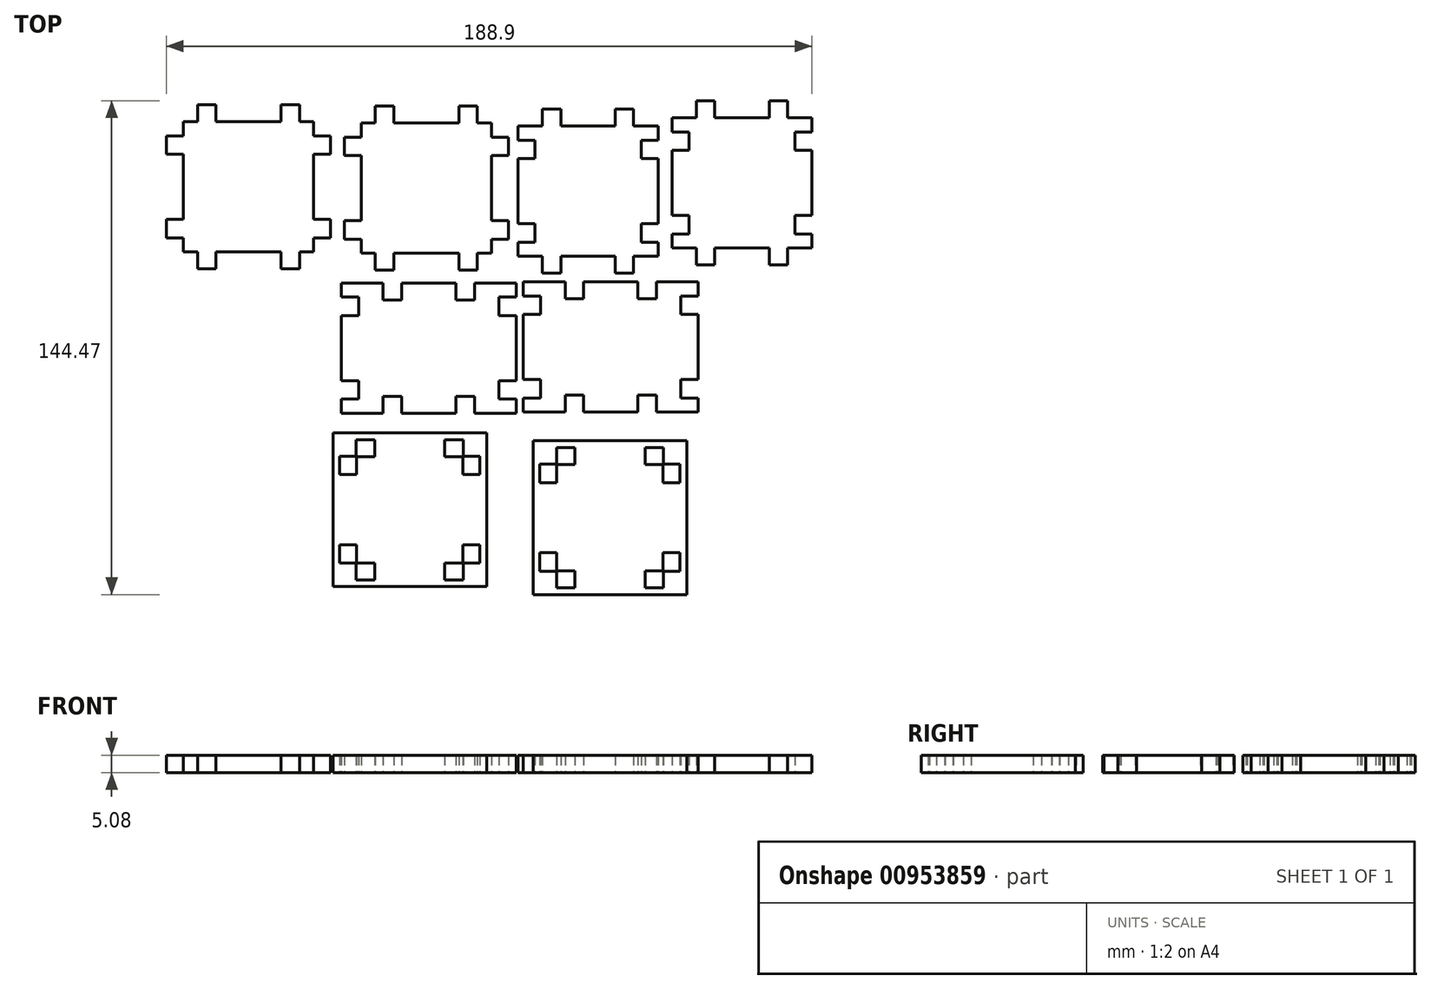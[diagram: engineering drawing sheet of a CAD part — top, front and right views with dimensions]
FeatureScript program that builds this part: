
annotation { "Feature Type Name" : "Feature", "Feature Type Description" : "" }
export const myFeature = defineFeature(function(context is Context, id is Id, definition is map)
    precondition{}
    {
        {
            var Q0;
            Q0=qCreatedBy(makeId("Top.planeOp"),FACE);
            var sketch = newSketch(context, id + "F0", { "sketchPlane" : qUnion([Q0])});
            skLineSegment(sketch, "E0", {"start": v(111.31, -90.9) * mm, "end": v(111.31, -90.9) * mm});
            skLineSegment(sketch, "E1", {"start": v(-309.98, -70.86) * mm, "end": v(-309.98, -70.86) * mm});
            skLineSegment(sketch, "E2", {"start": v(-261.6, -63.25) * mm, "end": v(-261.6, -63.25) * mm});
            skLineSegment(sketch, "E3", {"start": v(-306.4, -14.54) * mm, "end": v(-306.4, -14.54) * mm});
            skLineSegment(sketch, "E4", {"start": v(-50.36, 41.54) * mm, "end": v(-12.26, 41.54) * mm});
            skLineSegment(sketch, "E5", {"start": v(-12.26, 41.54) * mm, "end": v(-12.26, 79.64) * mm});
            skLineSegment(sketch, "E6", {"start": v(-50.36, 60.6) * mm, "end": v(-50.36, 79.64) * mm});
            skLineSegment(sketch, "E7", {"start": v(-50.36, 60.6) * mm, "end": v(-50.36, 41.54) * mm});
            skLineSegment(sketch, "E8", {"start": v(-50.36, 70.12) * mm, "end": v(-55.32, 70.12) * mm});
            skLineSegment(sketch, "E9", {"start": v(-55.32, 70.12) * mm, "end": v(-55.32, 75.52) * mm});
            skLineSegment(sketch, "E10", {"start": v(-55.32, 75.52) * mm, "end": v(-50.36, 75.52) * mm});
            skLineSegment(sketch, "E11", {"start": v(-50.36, 60.6) * mm, "end": v(-12.26, 60.6) * mm, "construction": true});
            skLineSegment(sketch, "E12", {"start": v(-31.31, 79.64) * mm, "end": v(-31.32, 41.54) * mm, "construction": true});
            skLineSegment(sketch, "E13.MirrorCS", {"start": v(-7.31, 70.11) * mm, "end": v(-7.31, 75.51) * mm});
            skLineSegment(sketch, "E14.MirrorCS", {"start": v(-7.31, 75.51) * mm, "end": v(-12.26, 75.51) * mm});
            skLineSegment(sketch, "E15.MirrorCS", {"start": v(-12.26, 70.12) * mm, "end": v(-7.31, 70.11) * mm});
            skLineSegment(sketch, "E16.MirrorCS", {"start": v(-12.27, 51.07) * mm, "end": v(-7.31, 51.07) * mm});
            skLineSegment(sketch, "E17.MirrorCS", {"start": v(-7.31, 45.67) * mm, "end": v(-12.27, 45.67) * mm});
            skLineSegment(sketch, "E18.MirrorCS", {"start": v(-7.31, 51.07) * mm, "end": v(-7.31, 45.67) * mm});
            skLineSegment(sketch, "E19.MirrorCS", {"start": v(-50.36, 51.07) * mm, "end": v(-55.32, 51.07) * mm});
            skLineSegment(sketch, "E20.MirrorCS", {"start": v(-55.32, 51.07) * mm, "end": v(-55.32, 45.67) * mm});
            skLineSegment(sketch, "E21.MirrorCS", {"start": v(-55.32, 45.67) * mm, "end": v(-50.37, 45.67) * mm});
            skLineSegment(sketch, "E22", {"start": v(-50.37, 45.67) * mm, "end": v(-50.36, 45.67) * mm});
            skLineSegment(sketch, "E23", {"start": v(-50.36, 51.07) * mm, "end": v(-50.36, 51.07) * mm});
            skLineSegment(sketch, "E24", {"start": v(-50.36, 79.64) * mm, "end": v(-31.31, 79.64) * mm});
            skLineSegment(sketch, "E25", {"start": v(-31.31, 79.64) * mm, "end": v(-12.26, 79.64) * mm});
            skLineSegment(sketch, "E26", {"start": v(-40.84, 79.64) * mm, "end": v(-40.84, 84.6) * mm});
            skLineSegment(sketch, "E27", {"start": v(-40.84, 84.6) * mm, "end": v(-46.24, 84.6) * mm});
            skLineSegment(sketch, "E28", {"start": v(-46.24, 84.6) * mm, "end": v(-46.24, 79.64) * mm});
            skLineSegment(sketch, "E29.MirrorCS", {"start": v(-21.79, 79.64) * mm, "end": v(-21.79, 84.6) * mm});
            skLineSegment(sketch, "E30.MirrorCS", {"start": v(-21.79, 84.6) * mm, "end": v(-16.39, 84.6) * mm});
            skLineSegment(sketch, "E31.MirrorCS", {"start": v(-16.39, 84.6) * mm, "end": v(-16.39, 79.64) * mm});
            skLineSegment(sketch, "E32.MirrorCS", {"start": v(-46.24, 36.59) * mm, "end": v(-46.24, 41.54) * mm});
            skLineSegment(sketch, "E33.MirrorCS", {"start": v(-40.84, 36.59) * mm, "end": v(-46.24, 36.59) * mm});
            skLineSegment(sketch, "E34.MirrorCS", {"start": v(-40.84, 41.54) * mm, "end": v(-40.84, 36.59) * mm});
            skLineSegment(sketch, "E35.MirrorCS", {"start": v(-21.8, 41.54) * mm, "end": v(-21.8, 36.59) * mm});
            skLineSegment(sketch, "E36.MirrorCS", {"start": v(-21.8, 36.59) * mm, "end": v(-16.4, 36.59) * mm});
            skLineSegment(sketch, "E37.MirrorCS", {"start": v(-16.4, 36.59) * mm, "end": v(-16.4, 41.54) * mm});
            skLineSegment(sketch, "E38", {"start": v(-46.24, 41.54) * mm, "end": v(-46.24, 41.54) * mm});
            skLineSegment(sketch, "E39", {"start": v(-40.84, 41.54) * mm, "end": v(-40.84, 41.54) * mm});
            skLineSegment(sketch, "E40", {"start": v(-21.8, 41.54) * mm, "end": v(-21.8, 41.54) * mm});
            skLineSegment(sketch, "E41", {"start": v(-16.4, 41.54) * mm, "end": v(-16.4, 41.54) * mm});
            skLineSegment(sketch, "E42", {"start": v(-102.38, 41.95) * mm, "end": v(-64.28, 41.94) * mm});
            skLineSegment(sketch, "E43", {"start": v(-64.28, 41.94) * mm, "end": v(-64.28, 80.05) * mm});
            skLineSegment(sketch, "E44", {"start": v(-102.38, 61) * mm, "end": v(-102.38, 80.05) * mm});
            skLineSegment(sketch, "E45", {"start": v(-102.38, 61) * mm, "end": v(-102.38, 41.95) * mm});
            skLineSegment(sketch, "E46", {"start": v(-102.38, 70.52) * mm, "end": v(-107.33, 70.52) * mm});
            skLineSegment(sketch, "E47", {"start": v(-107.33, 70.52) * mm, "end": v(-107.33, 75.92) * mm});
            skLineSegment(sketch, "E48", {"start": v(-107.33, 75.92) * mm, "end": v(-102.38, 75.92) * mm});
            skLineSegment(sketch, "E49", {"start": v(-102.38, 61) * mm, "end": v(-64.28, 61) * mm, "construction": true});
            skLineSegment(sketch, "E50", {"start": v(-83.33, 80.05) * mm, "end": v(-83.33, 41.95) * mm, "construction": true});
            skLineSegment(sketch, "E51.MirrorCS", {"start": v(-59.33, 70.52) * mm, "end": v(-59.33, 75.92) * mm});
            skLineSegment(sketch, "E52.MirrorCS", {"start": v(-59.33, 75.92) * mm, "end": v(-64.28, 75.92) * mm});
            skLineSegment(sketch, "E53.MirrorCS", {"start": v(-64.28, 70.52) * mm, "end": v(-59.33, 70.52) * mm});
            skLineSegment(sketch, "E54.MirrorCS", {"start": v(-64.28, 51.47) * mm, "end": v(-59.33, 51.47) * mm});
            skLineSegment(sketch, "E55.MirrorCS", {"start": v(-59.33, 46.07) * mm, "end": v(-64.28, 46.07) * mm});
            skLineSegment(sketch, "E56.MirrorCS", {"start": v(-59.33, 51.47) * mm, "end": v(-59.33, 46.07) * mm});
            skLineSegment(sketch, "E57.MirrorCS", {"start": v(-102.38, 51.47) * mm, "end": v(-107.34, 51.47) * mm});
            skLineSegment(sketch, "E58.MirrorCS", {"start": v(-107.34, 51.47) * mm, "end": v(-107.34, 46.07) * mm});
            skLineSegment(sketch, "E59.MirrorCS", {"start": v(-107.34, 46.07) * mm, "end": v(-102.38, 46.07) * mm});
            skLineSegment(sketch, "E60", {"start": v(-102.38, 46.07) * mm, "end": v(-102.38, 46.07) * mm});
            skLineSegment(sketch, "E61", {"start": v(-102.38, 51.47) * mm, "end": v(-102.38, 51.47) * mm});
            skLineSegment(sketch, "E62", {"start": v(-102.38, 80.05) * mm, "end": v(-83.33, 80.05) * mm});
            skLineSegment(sketch, "E63", {"start": v(-83.33, 80.05) * mm, "end": v(-64.28, 80.05) * mm});
            skLineSegment(sketch, "E64", {"start": v(-92.86, 80.05) * mm, "end": v(-92.86, 85) * mm});
            skLineSegment(sketch, "E65", {"start": v(-92.86, 85) * mm, "end": v(-98.26, 85) * mm});
            skLineSegment(sketch, "E66", {"start": v(-98.26, 85) * mm, "end": v(-98.26, 80.05) * mm});
            skLineSegment(sketch, "E67.MirrorCS", {"start": v(-73.8, 80.04) * mm, "end": v(-73.8, 85) * mm});
            skLineSegment(sketch, "E68.MirrorCS", {"start": v(-73.8, 85) * mm, "end": v(-68.4, 85) * mm});
            skLineSegment(sketch, "E69.MirrorCS", {"start": v(-68.4, 85) * mm, "end": v(-68.4, 80.04) * mm});
            skLineSegment(sketch, "E70.MirrorCS", {"start": v(-98.26, 37) * mm, "end": v(-98.26, 41.94) * mm});
            skLineSegment(sketch, "E71.MirrorCS", {"start": v(-92.86, 37) * mm, "end": v(-98.26, 37) * mm});
            skLineSegment(sketch, "E72.MirrorCS", {"start": v(-92.86, 41.94) * mm, "end": v(-92.86, 37) * mm});
            skLineSegment(sketch, "E73.MirrorCS", {"start": v(-73.8, 41.94) * mm, "end": v(-73.8, 36.99) * mm});
            skLineSegment(sketch, "E74.MirrorCS", {"start": v(-73.8, 36.99) * mm, "end": v(-68.4, 36.99) * mm});
            skLineSegment(sketch, "E75.MirrorCS", {"start": v(-68.4, 36.99) * mm, "end": v(-68.4, 41.94) * mm});
            skLineSegment(sketch, "E76", {"start": v(-98.26, 41.94) * mm, "end": v(-98.26, 41.95) * mm});
            skLineSegment(sketch, "E77", {"start": v(-92.86, 41.94) * mm, "end": v(-92.86, 41.95) * mm});
            skLineSegment(sketch, "E78", {"start": v(-73.8, 41.94) * mm, "end": v(-73.8, 41.95) * mm});
            skLineSegment(sketch, "E79", {"start": v(-68.4, 41.94) * mm, "end": v(-68.4, 41.94) * mm});
            skPoint(sketch, "E80.end.orphan", {"position": v(-93.44, 35.26) * mm});
            skPoint(sketch, "E81.end.orphan", {"position": v(-88.04, 35.26) * mm});
            skPoint(sketch, "E82.MirrorCS.end.orphan", {"position": v(-72.14, 35.26) * mm});
            skPoint(sketch, "E83.MirrorCS.end.orphan", {"position": v(-66.74, 35.26) * mm});
            skPoint(sketch, "E84.MirrorCS.end.orphan", {"position": v(-88.04, -12.75) * mm});
            skPoint(sketch, "E85.MirrorCS.end.orphan", {"position": v(-93.44, -12.75) * mm});
            skPoint(sketch, "E86.MirrorCS.end.orphan", {"position": v(-72.14, -12.75) * mm});
            skPoint(sketch, "E87.MirrorCS.end.orphan", {"position": v(-66.74, -12.75) * mm});
            skPoint(sketch, "E88.end.orphan", {"position": v(-47.44, 38.96) * mm});
            skPoint(sketch, "E89.end.orphan", {"position": v(-42.04, 38.96) * mm});
            skPoint(sketch, "E90.MirrorCS.end.orphan", {"position": v(-26.14, 38.96) * mm});
            skPoint(sketch, "E91.MirrorCS.end.orphan", {"position": v(-20.74, 38.96) * mm});
            skLineSegment(sketch, "E92", {"start": v(-51.08, -5.23) * mm, "end": v(-10.08, -5.23) * mm});
            skLineSegment(sketch, "E93", {"start": v(-51.08, 32.87) * mm, "end": v(-10.08, 32.87) * mm});
            skLineSegment(sketch, "E94", {"start": v(-10.08, 28.75) * mm, "end": v(-10.08, 23.35) * mm});
            skLineSegment(sketch, "E95", {"start": v(-51.08, 32.87) * mm, "end": v(-46.48, 32.87) * mm});
            skLineSegment(sketch, "E96", {"start": v(-14.68, 32.87) * mm, "end": v(-10.08, 32.87) * mm});
            skLineSegment(sketch, "E97", {"start": v(-46.48, 32.87) * mm, "end": v(-30.58, 32.87) * mm});
            skLineSegment(sketch, "E98", {"start": v(-30.58, 32.87) * mm, "end": v(-14.68, 32.87) * mm});
            skLineSegment(sketch, "E99", {"start": v(-30.58, 32.87) * mm, "end": v(-30.58, -5.23) * mm, "construction": true});
            skLineSegment(sketch, "E100", {"start": v(-51.08, 13.82) * mm, "end": v(-10.08, 13.82) * mm, "construction": true});
            skLineSegment(sketch, "E101.MirrorCS", {"start": v(-38.53, 32.87) * mm, "end": v(-38.53, 27.92) * mm});
            skLineSegment(sketch, "E102.MirrorCS", {"start": v(-43.93, 27.92) * mm, "end": v(-43.93, 32.87) * mm});
            skLineSegment(sketch, "E103.MirrorCS", {"start": v(-38.53, 27.92) * mm, "end": v(-43.93, 27.92) * mm});
            skLineSegment(sketch, "E104.MirrorCS", {"start": v(-22.63, 32.87) * mm, "end": v(-22.63, 27.92) * mm});
            skLineSegment(sketch, "E105.MirrorCS", {"start": v(-22.63, 27.92) * mm, "end": v(-17.23, 27.92) * mm});
            skLineSegment(sketch, "E106.MirrorCS", {"start": v(-17.23, 27.92) * mm, "end": v(-17.23, 32.87) * mm});
            skPoint(sketch, "E107.end.orphan", {"position": v(-43.93, 32.87) * mm});
            skPoint(sketch, "E108.end.orphan", {"position": v(-43.93, 37.83) * mm});
            skPoint(sketch, "E109.end.orphan", {"position": v(-38.53, 37.83) * mm});
            skPoint(sketch, "E109.start.orphan", {"position": v(-38.53, 32.87) * mm});
            skPoint(sketch, "E110.MirrorCS.end.orphan", {"position": v(-22.63, 37.83) * mm});
            skPoint(sketch, "E110.MirrorCS.start.orphan", {"position": v(-22.63, 32.87) * mm});
            skPoint(sketch, "E111.MirrorCS.end.orphan", {"position": v(-17.23, 37.83) * mm});
            skPoint(sketch, "E112.MirrorCS.end.orphan", {"position": v(-17.23, 32.87) * mm});
            skPoint(sketch, "E113.MirrorCS.end.orphan", {"position": v(-38.53, -10.18) * mm});
            skPoint(sketch, "E113.MirrorCS.start.orphan", {"position": v(-38.53, -5.23) * mm});
            skPoint(sketch, "E114.MirrorCS.end.orphan", {"position": v(-43.93, -10.18) * mm});
            skPoint(sketch, "E115.MirrorCS.end.orphan", {"position": v(-43.93, -5.23) * mm});
            skPoint(sketch, "E116.MirrorCS.end.orphan", {"position": v(-22.63, -10.18) * mm});
            skPoint(sketch, "E116.MirrorCS.start.orphan", {"position": v(-22.63, -5.23) * mm});
            skPoint(sketch, "E117.MirrorCS.end.orphan", {"position": v(-17.23, -10.18) * mm});
            skPoint(sketch, "E118.MirrorCS.end.orphan", {"position": v(-17.23, -5.23) * mm});
            skLineSegment(sketch, "E119.MirrorCS", {"start": v(-38.53, -5.23) * mm, "end": v(-38.53, -0.27) * mm});
            skLineSegment(sketch, "E120.MirrorCS", {"start": v(-38.53, -0.27) * mm, "end": v(-43.93, -0.27) * mm});
            skLineSegment(sketch, "E121.MirrorCS", {"start": v(-43.93, -0.27) * mm, "end": v(-43.93, -5.23) * mm});
            skLineSegment(sketch, "E122.MirrorCS", {"start": v(-22.63, -5.23) * mm, "end": v(-22.63, -0.27) * mm});
            skLineSegment(sketch, "E123.MirrorCS", {"start": v(-22.63, -0.27) * mm, "end": v(-17.23, -0.27) * mm});
            skLineSegment(sketch, "E124.MirrorCS", {"start": v(-17.23, -0.27) * mm, "end": v(-17.23, -5.23) * mm});
            skLineSegment(sketch, "E125", {"start": v(-51.08, 23.35) * mm, "end": v(-51.08, 28.75) * mm});
            skLineSegment(sketch, "E126", {"start": v(-51.08, 4.3) * mm, "end": v(-51.08, -1.1) * mm});
            skLineSegment(sketch, "E127", {"start": v(-4.5, 40.66) * mm, "end": v(36.5, 40.66) * mm});
            skLineSegment(sketch, "E128", {"start": v(-4.5, 78.76) * mm, "end": v(36.5, 78.76) * mm});
            skLineSegment(sketch, "E129", {"start": v(36.5, 78.76) * mm, "end": v(36.5, 40.66) * mm});
            skLineSegment(sketch, "E130", {"start": v(-4.5, 78.76) * mm, "end": v(0.1, 78.76) * mm});
            skLineSegment(sketch, "E131", {"start": v(31.9, 78.76) * mm, "end": v(36.5, 78.76) * mm});
            skLineSegment(sketch, "E132", {"start": v(0.1, 78.76) * mm, "end": v(16, 78.76) * mm});
            skLineSegment(sketch, "E133", {"start": v(16, 78.76) * mm, "end": v(31.9, 78.76) * mm});
            skLineSegment(sketch, "E134", {"start": v(16, 78.76) * mm, "end": v(16, 40.66) * mm, "construction": true});
            skLineSegment(sketch, "E135", {"start": v(-4.5, 59.71) * mm, "end": v(36.5, 59.71) * mm, "construction": true});
            skPoint(sketch, "E136.end.orphan", {"position": v(2.66, 78.76) * mm});
            skPoint(sketch, "E137.start.orphan", {"position": v(8.06, 78.76) * mm});
            skPoint(sketch, "E138.MirrorCS.start.orphan", {"position": v(23.96, 78.76) * mm});
            skPoint(sketch, "E139.MirrorCS.end.orphan", {"position": v(29.36, 78.76) * mm});
            skPoint(sketch, "E140.MirrorCS.end.orphan", {"position": v(8.06, 35.7) * mm});
            skPoint(sketch, "E140.MirrorCS.start.orphan", {"position": v(8.06, 40.66) * mm});
            skPoint(sketch, "E141.MirrorCS.end.orphan", {"position": v(2.66, 35.7) * mm});
            skPoint(sketch, "E142.MirrorCS.end.orphan", {"position": v(2.66, 40.66) * mm});
            skPoint(sketch, "E143.MirrorCS.end.orphan", {"position": v(23.96, 35.7) * mm});
            skPoint(sketch, "E143.MirrorCS.start.orphan", {"position": v(23.96, 40.66) * mm});
            skPoint(sketch, "E144.MirrorCS.end.orphan", {"position": v(29.36, 35.7) * mm});
            skPoint(sketch, "E145.MirrorCS.end.orphan", {"position": v(29.36, 40.66) * mm});
            skLineSegment(sketch, "E146", {"start": v(-4.5, 59.71) * mm, "end": v(-4.5, 78.76) * mm});
            skLineSegment(sketch, "E147", {"start": v(-4.5, 59.71) * mm, "end": v(-4.5, 40.66) * mm});
            skLineSegment(sketch, "E148", {"start": v(-4.5, 69.24) * mm, "end": v(0.46, 69.24) * mm});
            skLineSegment(sketch, "E149", {"start": v(0.46, 69.24) * mm, "end": v(0.46, 74.64) * mm});
            skLineSegment(sketch, "E150", {"start": v(0.46, 74.64) * mm, "end": v(-4.5, 74.64) * mm});
            skLineSegment(sketch, "E151.MirrorCS", {"start": v(-4.5, 50.19) * mm, "end": v(0.46, 50.19) * mm});
            skLineSegment(sketch, "E152.MirrorCS", {"start": v(0.46, 50.19) * mm, "end": v(0.46, 44.79) * mm});
            skLineSegment(sketch, "E153.MirrorCS", {"start": v(0.46, 44.79) * mm, "end": v(-4.5, 44.79) * mm});
            skLineSegment(sketch, "E154.MirrorCS", {"start": v(36.5, 69.24) * mm, "end": v(31.56, 69.24) * mm});
            skLineSegment(sketch, "E155.MirrorCS", {"start": v(31.56, 69.24) * mm, "end": v(31.56, 74.64) * mm});
            skLineSegment(sketch, "E156.MirrorCS", {"start": v(31.56, 74.64) * mm, "end": v(36.5, 74.64) * mm});
            skLineSegment(sketch, "E157.MirrorCS", {"start": v(36.5, 50.19) * mm, "end": v(31.56, 50.19) * mm});
            skLineSegment(sketch, "E158.MirrorCS", {"start": v(31.56, 50.19) * mm, "end": v(31.56, 44.79) * mm});
            skLineSegment(sketch, "E159.MirrorCS", {"start": v(31.56, 44.79) * mm, "end": v(36.5, 44.79) * mm});
            skLineSegment(sketch, "E160.MirrorCS", {"start": v(2.66, 83.72) * mm, "end": v(2.66, 78.76) * mm});
            skLineSegment(sketch, "E161.MirrorCS", {"start": v(8.06, 83.72) * mm, "end": v(2.66, 83.72) * mm});
            skLineSegment(sketch, "E162.MirrorCS", {"start": v(8.06, 78.76) * mm, "end": v(8.06, 83.72) * mm});
            skLineSegment(sketch, "E163.MirrorCS", {"start": v(23.96, 78.76) * mm, "end": v(23.96, 83.72) * mm});
            skLineSegment(sketch, "E164.MirrorCS", {"start": v(23.96, 83.72) * mm, "end": v(29.36, 83.72) * mm});
            skLineSegment(sketch, "E165.MirrorCS", {"start": v(29.36, 83.72) * mm, "end": v(29.36, 78.76) * mm});
            skPoint(sketch, "E166.MirrorCS.start.orphan", {"position": v(2.66, 73.8) * mm});
            skPoint(sketch, "E167.MirrorCS.start.orphan", {"position": v(8.06, 73.8) * mm});
            skPoint(sketch, "E168.MirrorCS.end.orphan", {"position": v(23.96, 73.8) * mm});
            skPoint(sketch, "E169.MirrorCS.end.orphan", {"position": v(29.36, 73.8) * mm});
            skLineSegment(sketch, "E170.MirrorCS", {"start": v(8.06, 40.66) * mm, "end": v(8.06, 35.7) * mm});
            skLineSegment(sketch, "E171.MirrorCS", {"start": v(8.06, 35.7) * mm, "end": v(2.66, 35.7) * mm});
            skLineSegment(sketch, "E172.MirrorCS", {"start": v(2.66, 35.7) * mm, "end": v(2.66, 40.66) * mm});
            skLineSegment(sketch, "E173.MirrorCS", {"start": v(23.96, 40.66) * mm, "end": v(23.96, 35.7) * mm});
            skLineSegment(sketch, "E174.MirrorCS", {"start": v(23.96, 35.7) * mm, "end": v(29.36, 35.7) * mm});
            skLineSegment(sketch, "E175.MirrorCS", {"start": v(29.36, 35.7) * mm, "end": v(29.36, 40.66) * mm});
            skPoint(sketch, "E176.MirrorCS.start.orphan", {"position": v(2.66, 45.62) * mm});
            skPoint(sketch, "E177.MirrorCS.start.orphan", {"position": v(8.06, 45.62) * mm});
            skPoint(sketch, "E178.MirrorCS.end.orphan", {"position": v(23.96, 45.62) * mm});
            skPoint(sketch, "E179.MirrorCS.start.orphan", {"position": v(29.36, 45.62) * mm});
            skLineSegment(sketch, "E180", {"start": v(40.56, 43.1) * mm, "end": v(81.56, 43.1) * mm});
            skLineSegment(sketch, "E181", {"start": v(40.56, 81.2) * mm, "end": v(81.56, 81.2) * mm});
            skLineSegment(sketch, "E182", {"start": v(81.56, 81.2) * mm, "end": v(81.56, 43.1) * mm});
            skLineSegment(sketch, "E183", {"start": v(40.56, 81.2) * mm, "end": v(45.16, 81.2) * mm});
            skLineSegment(sketch, "E184", {"start": v(76.96, 81.2) * mm, "end": v(81.56, 81.2) * mm});
            skLineSegment(sketch, "E185", {"start": v(45.16, 81.2) * mm, "end": v(61.06, 81.2) * mm});
            skLineSegment(sketch, "E186", {"start": v(61.06, 81.2) * mm, "end": v(76.96, 81.2) * mm});
            skLineSegment(sketch, "E187", {"start": v(61.06, 81.2) * mm, "end": v(61.06, 43.1) * mm, "construction": true});
            skLineSegment(sketch, "E188", {"start": v(40.56, 62.15) * mm, "end": v(81.56, 62.15) * mm, "construction": true});
            skPoint(sketch, "E189.end.orphan", {"position": v(47.7, 81.2) * mm});
            skPoint(sketch, "E190.start.orphan", {"position": v(53.1, 81.2) * mm});
            skPoint(sketch, "E191.MirrorCS.start.orphan", {"position": v(69, 81.2) * mm});
            skPoint(sketch, "E192.MirrorCS.end.orphan", {"position": v(74.4, 81.2) * mm});
            skPoint(sketch, "E193.MirrorCS.end.orphan", {"position": v(53.1, 38.14) * mm});
            skPoint(sketch, "E193.MirrorCS.start.orphan", {"position": v(53.1, 43.1) * mm});
            skPoint(sketch, "E194.MirrorCS.end.orphan", {"position": v(47.7, 38.14) * mm});
            skPoint(sketch, "E195.MirrorCS.end.orphan", {"position": v(47.7, 43.1) * mm});
            skPoint(sketch, "E196.MirrorCS.end.orphan", {"position": v(69, 38.14) * mm});
            skPoint(sketch, "E196.MirrorCS.start.orphan", {"position": v(69, 43.1) * mm});
            skPoint(sketch, "E197.MirrorCS.end.orphan", {"position": v(74.4, 38.14) * mm});
            skPoint(sketch, "E198.MirrorCS.end.orphan", {"position": v(74.4, 43.1) * mm});
            skLineSegment(sketch, "E199", {"start": v(40.56, 62.15) * mm, "end": v(40.56, 81.2) * mm});
            skLineSegment(sketch, "E200", {"start": v(40.56, 62.15) * mm, "end": v(40.56, 43.1) * mm});
            skLineSegment(sketch, "E201", {"start": v(40.56, 71.67) * mm, "end": v(45.5, 71.67) * mm});
            skLineSegment(sketch, "E202", {"start": v(45.5, 71.67) * mm, "end": v(45.5, 77.07) * mm});
            skLineSegment(sketch, "E203", {"start": v(45.5, 77.07) * mm, "end": v(40.56, 77.07) * mm});
            skLineSegment(sketch, "E204.MirrorCS", {"start": v(40.56, 52.62) * mm, "end": v(45.5, 52.62) * mm});
            skLineSegment(sketch, "E205.MirrorCS", {"start": v(45.5, 52.62) * mm, "end": v(45.5, 47.22) * mm});
            skLineSegment(sketch, "E206.MirrorCS", {"start": v(45.5, 47.22) * mm, "end": v(40.56, 47.22) * mm});
            skLineSegment(sketch, "E207.MirrorCS", {"start": v(81.56, 71.67) * mm, "end": v(76.6, 71.67) * mm});
            skLineSegment(sketch, "E208.MirrorCS", {"start": v(76.6, 71.67) * mm, "end": v(76.6, 77.07) * mm});
            skLineSegment(sketch, "E209.MirrorCS", {"start": v(76.6, 77.07) * mm, "end": v(81.56, 77.07) * mm});
            skLineSegment(sketch, "E210.MirrorCS", {"start": v(81.56, 52.62) * mm, "end": v(76.6, 52.62) * mm});
            skLineSegment(sketch, "E211.MirrorCS", {"start": v(76.6, 52.62) * mm, "end": v(76.6, 47.22) * mm});
            skLineSegment(sketch, "E212.MirrorCS", {"start": v(76.6, 47.22) * mm, "end": v(81.56, 47.22) * mm});
            skLineSegment(sketch, "E213.MirrorCS", {"start": v(47.7, 86.15) * mm, "end": v(47.7, 81.2) * mm});
            skLineSegment(sketch, "E214.MirrorCS", {"start": v(53.1, 86.15) * mm, "end": v(47.7, 86.15) * mm});
            skLineSegment(sketch, "E215.MirrorCS", {"start": v(53.1, 81.2) * mm, "end": v(53.1, 86.15) * mm});
            skLineSegment(sketch, "E216.MirrorCS", {"start": v(69, 81.2) * mm, "end": v(69, 86.15) * mm});
            skLineSegment(sketch, "E217.MirrorCS", {"start": v(69, 86.15) * mm, "end": v(74.4, 86.15) * mm});
            skLineSegment(sketch, "E218.MirrorCS", {"start": v(74.4, 86.15) * mm, "end": v(74.4, 81.2) * mm});
            skPoint(sketch, "E219.MirrorCS.start.orphan", {"position": v(47.7, 76.24) * mm});
            skPoint(sketch, "E220.MirrorCS.start.orphan", {"position": v(53.1, 76.24) * mm});
            skPoint(sketch, "E221.MirrorCS.end.orphan", {"position": v(69, 76.24) * mm});
            skPoint(sketch, "E222.MirrorCS.end.orphan", {"position": v(74.4, 76.24) * mm});
            skLineSegment(sketch, "E223.MirrorCS", {"start": v(53.1, 43.1) * mm, "end": v(53.1, 38.14) * mm});
            skLineSegment(sketch, "E224.MirrorCS", {"start": v(53.1, 38.14) * mm, "end": v(47.7, 38.14) * mm});
            skLineSegment(sketch, "E225.MirrorCS", {"start": v(47.7, 38.14) * mm, "end": v(47.7, 43.1) * mm});
            skLineSegment(sketch, "E226.MirrorCS", {"start": v(69, 43.1) * mm, "end": v(69, 38.14) * mm});
            skLineSegment(sketch, "E227.MirrorCS", {"start": v(69, 38.14) * mm, "end": v(74.4, 38.14) * mm});
            skLineSegment(sketch, "E228.MirrorCS", {"start": v(74.4, 38.14) * mm, "end": v(74.4, 43.1) * mm});
            skPoint(sketch, "E229.MirrorCS.start.orphan", {"position": v(47.7, 48.05) * mm});
            skPoint(sketch, "E230.MirrorCS.start.orphan", {"position": v(53.1, 48.05) * mm});
            skPoint(sketch, "E231.MirrorCS.end.orphan", {"position": v(69, 48.05) * mm});
            skPoint(sketch, "E232.MirrorCS.start.orphan", {"position": v(74.4, 48.05) * mm});
            skLineSegment(sketch, "E233", {"start": v(-51.08, 32.87) * mm, "end": v(-56.16, 32.87) * mm});
            skLineSegment(sketch, "E234", {"start": v(-56.16, 32.87) * mm, "end": v(-56.16, -5.23) * mm});
            skLineSegment(sketch, "E235", {"start": v(-56.16, -5.23) * mm, "end": v(-51.08, -5.23) * mm});
            skLineSegment(sketch, "E236", {"start": v(-51.08, -1.1) * mm, "end": v(-56.16, -1.1) * mm});
            skLineSegment(sketch, "E237", {"start": v(-51.08, 4.3) * mm, "end": v(-56.16, 4.3) * mm});
            skLineSegment(sketch, "E238", {"start": v(-51.08, 23.35) * mm, "end": v(-56.16, 23.35) * mm});
            skLineSegment(sketch, "E239", {"start": v(-51.08, 28.75) * mm, "end": v(-56.16, 28.75) * mm});
            skPoint(sketch, "E240.end.orphan", {"position": v(-46.13, 28.75) * mm});
            skPoint(sketch, "E241.end.orphan", {"position": v(-46.13, 23.35) * mm});
            skPoint(sketch, "E242.MirrorCS.end.orphan", {"position": v(-46.13, 4.3) * mm});
            skPoint(sketch, "E243.MirrorCS.end.orphan", {"position": v(-51.08, -1.1) * mm});
            skPoint(sketch, "E243.MirrorCS.start.orphan", {"position": v(-46.13, -1.1) * mm});
            skPoint(sketch, "E244.MirrorCS.end.orphan", {"position": v(-10.08, 28.75) * mm});
            skPoint(sketch, "E244.MirrorCS.start.orphan", {"position": v(-15.04, 28.75) * mm});
            skPoint(sketch, "E245.MirrorCS.start.orphan", {"position": v(-15.04, 23.35) * mm});
            skPoint(sketch, "E246.MirrorCS.start.orphan", {"position": v(-10.08, 23.35) * mm});
            skPoint(sketch, "E247.MirrorCS.end.orphan", {"position": v(-15.04, 4.3) * mm});
            skPoint(sketch, "E247.MirrorCS.start.orphan", {"position": v(-10.08, 4.3) * mm});
            skPoint(sketch, "E248.MirrorCS.end.orphan", {"position": v(-15.04, -1.1) * mm});
            skPoint(sketch, "E249.MirrorCS.end.orphan", {"position": v(-10.08, -1.1) * mm});
            skLineSegment(sketch, "E250", {"start": v(-10.08, 32.87) * mm, "end": v(-5, 32.87) * mm});
            skLineSegment(sketch, "E251", {"start": v(-5, 32.87) * mm, "end": v(-5, -5.23) * mm});
            skLineSegment(sketch, "E252", {"start": v(-5, -5.23) * mm, "end": v(-10.08, -5.23) * mm});
            skLineSegment(sketch, "E253", {"start": v(-10.08, 28.75) * mm, "end": v(-5, 28.75) * mm});
            skLineSegment(sketch, "E254", {"start": v(-10.08, 23.35) * mm, "end": v(-5, 23.35) * mm});
            skLineSegment(sketch, "E255", {"start": v(-10.08, 4.3) * mm, "end": v(-5, 4.3) * mm});
            skLineSegment(sketch, "E256", {"start": v(-10.08, -1.1) * mm, "end": v(-5, -1.1) * mm});
            skLineSegment(sketch, "E257.trimOffspring", {"start": v(-10.08, 4.3) * mm, "end": v(-10.08, -1.1) * mm});
            skLineSegment(sketch, "E258", {"start": v(2.17, -4.94) * mm, "end": v(43.17, -4.94) * mm});
            skLineSegment(sketch, "E259", {"start": v(2.17, 33.16) * mm, "end": v(43.17, 33.16) * mm});
            skLineSegment(sketch, "E260", {"start": v(43.17, 29.04) * mm, "end": v(43.17, 23.64) * mm});
            skLineSegment(sketch, "E261", {"start": v(2.17, 33.16) * mm, "end": v(6.77, 33.16) * mm});
            skLineSegment(sketch, "E262", {"start": v(38.57, 33.16) * mm, "end": v(43.17, 33.16) * mm});
            skLineSegment(sketch, "E263", {"start": v(6.77, 33.16) * mm, "end": v(22.67, 33.16) * mm});
            skLineSegment(sketch, "E264", {"start": v(22.67, 33.16) * mm, "end": v(38.57, 33.16) * mm});
            skLineSegment(sketch, "E265", {"start": v(22.67, 33.16) * mm, "end": v(22.67, -4.94) * mm, "construction": true});
            skLineSegment(sketch, "E266", {"start": v(2.17, 14.11) * mm, "end": v(43.17, 14.11) * mm, "construction": true});
            skLineSegment(sketch, "E267.MirrorCS", {"start": v(14.72, 33.16) * mm, "end": v(14.72, 28.2) * mm});
            skLineSegment(sketch, "E268.MirrorCS", {"start": v(9.32, 28.2) * mm, "end": v(9.32, 33.16) * mm});
            skLineSegment(sketch, "E269.MirrorCS", {"start": v(14.72, 28.2) * mm, "end": v(9.32, 28.2) * mm});
            skLineSegment(sketch, "E270.MirrorCS", {"start": v(30.62, 33.16) * mm, "end": v(30.62, 28.2) * mm});
            skLineSegment(sketch, "E271.MirrorCS", {"start": v(30.62, 28.2) * mm, "end": v(36.02, 28.2) * mm});
            skLineSegment(sketch, "E272.MirrorCS", {"start": v(36.02, 28.2) * mm, "end": v(36.02, 33.16) * mm});
            skPoint(sketch, "E273.end.orphan", {"position": v(9.32, 33.16) * mm});
            skPoint(sketch, "E274.start.orphan", {"position": v(14.72, 33.16) * mm});
            skPoint(sketch, "E275.MirrorCS.start.orphan", {"position": v(30.62, 33.16) * mm});
            skPoint(sketch, "E276.MirrorCS.end.orphan", {"position": v(36.02, 33.16) * mm});
            skPoint(sketch, "E277.MirrorCS.start.orphan", {"position": v(14.72, -4.94) * mm});
            skPoint(sketch, "E278.MirrorCS.end.orphan", {"position": v(9.32, -4.94) * mm});
            skPoint(sketch, "E279.MirrorCS.start.orphan", {"position": v(30.62, -4.94) * mm});
            skPoint(sketch, "E280.MirrorCS.end.orphan", {"position": v(36.02, -4.94) * mm});
            skLineSegment(sketch, "E281.MirrorCS", {"start": v(14.72, -4.94) * mm, "end": v(14.72, 0.01) * mm});
            skLineSegment(sketch, "E282.MirrorCS", {"start": v(14.72, 0.01) * mm, "end": v(9.32, 0.01) * mm});
            skLineSegment(sketch, "E283.MirrorCS", {"start": v(9.32, 0.01) * mm, "end": v(9.32, -4.94) * mm});
            skLineSegment(sketch, "E284.MirrorCS", {"start": v(30.62, -4.94) * mm, "end": v(30.62, 0.01) * mm});
            skLineSegment(sketch, "E285.MirrorCS", {"start": v(30.62, 0.01) * mm, "end": v(36.02, 0.01) * mm});
            skLineSegment(sketch, "E286.MirrorCS", {"start": v(36.02, 0.01) * mm, "end": v(36.02, -4.94) * mm});
            skLineSegment(sketch, "E287", {"start": v(2.17, 23.64) * mm, "end": v(2.17, 29.04) * mm});
            skLineSegment(sketch, "E288", {"start": v(2.17, 4.59) * mm, "end": v(2.17, -0.81) * mm});
            skLineSegment(sketch, "E289", {"start": v(2.17, 33.16) * mm, "end": v(-2.91, 33.16) * mm});
            skLineSegment(sketch, "E290", {"start": v(-2.91, 33.16) * mm, "end": v(-2.91, -4.94) * mm});
            skLineSegment(sketch, "E291", {"start": v(-2.91, -4.94) * mm, "end": v(2.17, -4.94) * mm});
            skLineSegment(sketch, "E292", {"start": v(2.17, -0.81) * mm, "end": v(-2.91, -0.81) * mm});
            skLineSegment(sketch, "E293", {"start": v(2.17, 4.59) * mm, "end": v(-2.91, 4.59) * mm});
            skLineSegment(sketch, "E294", {"start": v(2.17, 23.64) * mm, "end": v(-2.91, 23.64) * mm});
            skLineSegment(sketch, "E295", {"start": v(2.17, 29.04) * mm, "end": v(-2.91, 29.04) * mm});
            skPoint(sketch, "E296.end.orphan", {"position": v(7.12, 29.04) * mm});
            skPoint(sketch, "E297.end.orphan", {"position": v(7.12, 23.64) * mm});
            skPoint(sketch, "E298.MirrorCS.end.orphan", {"position": v(7.12, 4.59) * mm});
            skPoint(sketch, "E299.MirrorCS.end.orphan", {"position": v(2.17, -0.81) * mm});
            skPoint(sketch, "E299.MirrorCS.start.orphan", {"position": v(7.12, -0.81) * mm});
            skPoint(sketch, "E300.MirrorCS.end.orphan", {"position": v(43.17, 29.04) * mm});
            skPoint(sketch, "E300.MirrorCS.start.orphan", {"position": v(38.22, 29.04) * mm});
            skPoint(sketch, "E301.MirrorCS.start.orphan", {"position": v(38.22, 23.64) * mm});
            skPoint(sketch, "E302.MirrorCS.start.orphan", {"position": v(43.17, 23.64) * mm});
            skPoint(sketch, "E303.MirrorCS.end.orphan", {"position": v(38.22, 4.59) * mm});
            skPoint(sketch, "E303.MirrorCS.start.orphan", {"position": v(43.17, 4.59) * mm});
            skPoint(sketch, "E304.MirrorCS.end.orphan", {"position": v(38.22, -0.81) * mm});
            skPoint(sketch, "E305.MirrorCS.end.orphan", {"position": v(43.17, -0.81) * mm});
            skLineSegment(sketch, "E306", {"start": v(43.17, 33.16) * mm, "end": v(48.25, 33.16) * mm});
            skLineSegment(sketch, "E307", {"start": v(48.25, 33.16) * mm, "end": v(48.25, -4.94) * mm});
            skLineSegment(sketch, "E308", {"start": v(48.25, -4.94) * mm, "end": v(43.17, -4.94) * mm});
            skLineSegment(sketch, "E309", {"start": v(43.17, 29.04) * mm, "end": v(48.25, 29.04) * mm});
            skLineSegment(sketch, "E310", {"start": v(43.17, 23.64) * mm, "end": v(48.25, 23.64) * mm});
            skLineSegment(sketch, "E311", {"start": v(43.17, 4.59) * mm, "end": v(48.25, 4.59) * mm});
            skLineSegment(sketch, "E312", {"start": v(43.17, -0.81) * mm, "end": v(48.25, -0.81) * mm});
            skLineSegment(sketch, "E313.trimOffspring", {"start": v(43.17, 4.59) * mm, "end": v(43.17, -0.81) * mm});
            skLineSegment(sketch, "E314", {"start": v(-56.63, -12.98) * mm, "end": v(-36.13, -12.98) * mm});
            skLineSegment(sketch, "E315", {"start": v(-36.13, -12.98) * mm, "end": v(-15.63, -12.98) * mm});
            skLineSegment(sketch, "E316", {"start": v(-15.63, -12.98) * mm, "end": v(-15.63, -33.48) * mm});
            skLineSegment(sketch, "E317", {"start": v(-15.63, -33.48) * mm, "end": v(-15.63, -53.98) * mm});
            skLineSegment(sketch, "E318", {"start": v(-15.63, -53.98) * mm, "end": v(-56.63, -53.98) * mm});
            skLineSegment(sketch, "E319", {"start": v(-56.63, -12.98) * mm, "end": v(-56.63, -53.98) * mm});
            skLineSegment(sketch, "E320", {"start": v(-25.88, -12.98) * mm, "end": v(-25.88, -17.94) * mm});
            skLineSegment(sketch, "E321", {"start": v(-25.88, -17.94) * mm, "end": v(-20.48, -17.94) * mm});
            skLineSegment(sketch, "E322", {"start": v(-20.48, -17.94) * mm, "end": v(-20.48, -12.98) * mm});
            skLineSegment(sketch, "E323", {"start": v(-15.63, -23.23) * mm, "end": v(-20.58, -23.23) * mm});
            skLineSegment(sketch, "E324", {"start": v(-20.58, -23.23) * mm, "end": v(-20.58, -17.83) * mm});
            skLineSegment(sketch, "E325", {"start": v(-20.58, -17.83) * mm, "end": v(-15.63, -17.83) * mm});
            skLineSegment(sketch, "E326", {"start": v(-36.13, -12.98) * mm, "end": v(-36.13, -53.98) * mm, "construction": true});
            skLineSegment(sketch, "E327", {"start": v(-56.63, -33.48) * mm, "end": v(-15.63, -33.48) * mm, "construction": true});
            skLineSegment(sketch, "E328.MirrorCS", {"start": v(-15.63, -43.73) * mm, "end": v(-20.58, -43.73) * mm});
            skLineSegment(sketch, "E329.MirrorCS", {"start": v(-20.58, -43.73) * mm, "end": v(-20.58, -49.13) * mm});
            skLineSegment(sketch, "E330.MirrorCS", {"start": v(-20.58, -49.13) * mm, "end": v(-15.63, -49.13) * mm});
            skLineSegment(sketch, "E331.MirrorCS", {"start": v(-20.48, -49.03) * mm, "end": v(-20.48, -53.98) * mm});
            skLineSegment(sketch, "E332.MirrorCS", {"start": v(-25.88, -49.03) * mm, "end": v(-20.48, -49.03) * mm});
            skLineSegment(sketch, "E333.MirrorCS", {"start": v(-25.88, -53.98) * mm, "end": v(-25.88, -49.03) * mm});
            skLineSegment(sketch, "E334.MirrorCS", {"start": v(-46.38, -12.98) * mm, "end": v(-46.38, -17.94) * mm});
            skLineSegment(sketch, "E335.MirrorCS", {"start": v(-46.38, -17.94) * mm, "end": v(-51.78, -17.94) * mm});
            skLineSegment(sketch, "E336.MirrorCS", {"start": v(-51.78, -17.94) * mm, "end": v(-51.78, -12.98) * mm});
            skLineSegment(sketch, "E337.MirrorCS", {"start": v(-51.68, -23.23) * mm, "end": v(-51.68, -17.83) * mm});
            skLineSegment(sketch, "E338.MirrorCS", {"start": v(-51.68, -17.83) * mm, "end": v(-56.63, -17.83) * mm});
            skLineSegment(sketch, "E339.MirrorCS", {"start": v(-56.63, -23.23) * mm, "end": v(-51.68, -23.23) * mm});
            skLineSegment(sketch, "E340.MirrorCS", {"start": v(-46.38, -49.03) * mm, "end": v(-51.78, -49.03) * mm});
            skLineSegment(sketch, "E341.MirrorCS", {"start": v(-51.78, -49.03) * mm, "end": v(-51.78, -53.98) * mm});
            skLineSegment(sketch, "E342.MirrorCS", {"start": v(-46.38, -53.98) * mm, "end": v(-46.38, -49.03) * mm});
            skLineSegment(sketch, "E343.MirrorCS", {"start": v(-51.68, -43.73) * mm, "end": v(-51.68, -49.13) * mm});
            skLineSegment(sketch, "E344.MirrorCS", {"start": v(-56.63, -43.73) * mm, "end": v(-51.68, -43.73) * mm});
            skLineSegment(sketch, "E345.MirrorCS", {"start": v(-51.68, -49.13) * mm, "end": v(-56.63, -49.13) * mm});
            skLineSegment(sketch, "E346", {"start": v(-15.63, -12.98) * mm, "end": v(-15.63, -10.98) * mm});
            skLineSegment(sketch, "E347", {"start": v(-15.63, -10.98) * mm, "end": v(-56.63, -10.98) * mm});
            skLineSegment(sketch, "E348", {"start": v(-56.63, -10.98) * mm, "end": v(-56.63, -12.98) * mm});
            skLineSegment(sketch, "E349", {"start": v(-56.63, -10.98) * mm, "end": v(-58.63, -10.98) * mm});
            skLineSegment(sketch, "E350", {"start": v(-58.63, -10.98) * mm, "end": v(-58.63, -53.98) * mm});
            skLineSegment(sketch, "E351", {"start": v(-58.63, -53.98) * mm, "end": v(-56.63, -53.98) * mm});
            skLineSegment(sketch, "E352", {"start": v(-15.63, -10.98) * mm, "end": v(-13.63, -10.98) * mm});
            skLineSegment(sketch, "E353", {"start": v(-13.63, -10.98) * mm, "end": v(-13.63, -53.98) * mm});
            skLineSegment(sketch, "E354", {"start": v(-13.63, -53.98) * mm, "end": v(-15.63, -53.98) * mm});
            skLineSegment(sketch, "E355", {"start": v(-13.63, -53.98) * mm, "end": v(-13.63, -55.98) * mm});
            skLineSegment(sketch, "E356", {"start": v(-13.63, -55.98) * mm, "end": v(-58.63, -55.98) * mm});
            skLineSegment(sketch, "E357", {"start": v(-58.63, -55.98) * mm, "end": v(-58.63, -53.98) * mm});
            skPoint(sketch, "E358.MirrorCS.end.orphan", {"position": v(20.02, -12.51) * mm});
            skPoint(sketch, "E359.MirrorCS.end.orphan", {"position": v(14.62, -12.51) * mm});
            skPoint(sketch, "E360.MirrorCS.end.orphan", {"position": v(35.92, -12.51) * mm});
            skPoint(sketch, "E361.MirrorCS.end.orphan", {"position": v(41.32, -12.51) * mm});
            skLineSegment(sketch, "E362", {"start": v(1.93, -15.32) * mm, "end": v(22.43, -15.32) * mm});
            skLineSegment(sketch, "E363", {"start": v(22.43, -15.32) * mm, "end": v(42.93, -15.32) * mm});
            skLineSegment(sketch, "E364", {"start": v(42.93, -15.32) * mm, "end": v(42.93, -35.82) * mm});
            skLineSegment(sketch, "E365", {"start": v(42.93, -35.82) * mm, "end": v(42.93, -56.32) * mm});
            skLineSegment(sketch, "E366", {"start": v(42.93, -56.32) * mm, "end": v(1.93, -56.32) * mm});
            skLineSegment(sketch, "E367", {"start": v(1.93, -15.32) * mm, "end": v(1.93, -56.32) * mm});
            skLineSegment(sketch, "E368", {"start": v(32.68, -15.32) * mm, "end": v(32.68, -20.27) * mm});
            skLineSegment(sketch, "E369", {"start": v(32.68, -20.27) * mm, "end": v(38.08, -20.27) * mm});
            skLineSegment(sketch, "E370", {"start": v(38.08, -20.27) * mm, "end": v(38.08, -15.32) * mm});
            skLineSegment(sketch, "E371", {"start": v(42.93, -25.57) * mm, "end": v(37.98, -25.57) * mm});
            skLineSegment(sketch, "E372", {"start": v(37.98, -25.57) * mm, "end": v(37.98, -20.17) * mm});
            skLineSegment(sketch, "E373", {"start": v(37.98, -20.17) * mm, "end": v(42.93, -20.17) * mm});
            skLineSegment(sketch, "E374", {"start": v(22.43, -15.32) * mm, "end": v(22.43, -56.32) * mm, "construction": true});
            skLineSegment(sketch, "E375", {"start": v(1.93, -35.82) * mm, "end": v(42.93, -35.82) * mm, "construction": true});
            skLineSegment(sketch, "E376.MirrorCS", {"start": v(42.93, -46.07) * mm, "end": v(37.98, -46.07) * mm});
            skLineSegment(sketch, "E377.MirrorCS", {"start": v(37.98, -46.07) * mm, "end": v(37.98, -51.47) * mm});
            skLineSegment(sketch, "E378.MirrorCS", {"start": v(37.98, -51.47) * mm, "end": v(42.93, -51.47) * mm});
            skLineSegment(sketch, "E379.MirrorCS", {"start": v(38.08, -51.36) * mm, "end": v(38.08, -56.32) * mm});
            skLineSegment(sketch, "E380.MirrorCS", {"start": v(32.68, -51.36) * mm, "end": v(38.08, -51.36) * mm});
            skLineSegment(sketch, "E381.MirrorCS", {"start": v(32.68, -56.32) * mm, "end": v(32.68, -51.36) * mm});
            skLineSegment(sketch, "E382.MirrorCS", {"start": v(12.18, -15.32) * mm, "end": v(12.18, -20.27) * mm});
            skLineSegment(sketch, "E383.MirrorCS", {"start": v(12.18, -20.27) * mm, "end": v(6.78, -20.27) * mm});
            skLineSegment(sketch, "E384.MirrorCS", {"start": v(6.78, -20.27) * mm, "end": v(6.78, -15.32) * mm});
            skLineSegment(sketch, "E385.MirrorCS", {"start": v(6.88, -25.57) * mm, "end": v(6.88, -20.17) * mm});
            skLineSegment(sketch, "E386.MirrorCS", {"start": v(6.88, -20.17) * mm, "end": v(1.93, -20.17) * mm});
            skLineSegment(sketch, "E387.MirrorCS", {"start": v(1.93, -25.57) * mm, "end": v(6.88, -25.57) * mm});
            skLineSegment(sketch, "E388.MirrorCS", {"start": v(12.18, -51.36) * mm, "end": v(6.78, -51.36) * mm});
            skLineSegment(sketch, "E389.MirrorCS", {"start": v(6.78, -51.36) * mm, "end": v(6.78, -56.32) * mm});
            skLineSegment(sketch, "E390.MirrorCS", {"start": v(12.18, -56.32) * mm, "end": v(12.18, -51.36) * mm});
            skLineSegment(sketch, "E391.MirrorCS", {"start": v(6.88, -46.07) * mm, "end": v(6.88, -51.47) * mm});
            skLineSegment(sketch, "E392.MirrorCS", {"start": v(1.93, -46.07) * mm, "end": v(6.88, -46.07) * mm});
            skLineSegment(sketch, "E393.MirrorCS", {"start": v(6.88, -51.47) * mm, "end": v(1.93, -51.47) * mm});
            skLineSegment(sketch, "E394", {"start": v(42.93, -15.32) * mm, "end": v(42.93, -13.32) * mm});
            skLineSegment(sketch, "E395", {"start": v(42.93, -13.32) * mm, "end": v(1.93, -13.32) * mm});
            skLineSegment(sketch, "E396", {"start": v(1.93, -13.32) * mm, "end": v(1.93, -15.32) * mm});
            skLineSegment(sketch, "E397", {"start": v(1.93, -13.32) * mm, "end": v(-0.07, -13.32) * mm});
            skLineSegment(sketch, "E398", {"start": v(-0.07, -13.32) * mm, "end": v(-0.07, -56.32) * mm});
            skLineSegment(sketch, "E399", {"start": v(-0.07, -56.32) * mm, "end": v(1.93, -56.32) * mm});
            skLineSegment(sketch, "E400", {"start": v(42.93, -13.32) * mm, "end": v(44.93, -13.32) * mm});
            skLineSegment(sketch, "E401", {"start": v(44.93, -13.32) * mm, "end": v(44.93, -56.32) * mm});
            skLineSegment(sketch, "E402", {"start": v(44.93, -56.32) * mm, "end": v(42.93, -56.32) * mm});
            skLineSegment(sketch, "E403", {"start": v(44.93, -56.32) * mm, "end": v(44.93, -58.32) * mm});
            skLineSegment(sketch, "E404", {"start": v(44.93, -58.32) * mm, "end": v(-0.07, -58.32) * mm});
            skLineSegment(sketch, "E405", {"start": v(-0.07, -58.32) * mm, "end": v(-0.07, -56.32) * mm});
            skSolve(sketch);
        }
        {
            var Q0;
            Q0=makeQuery(id+"F0.imprint","IMPRINT",FACE,{"disambiguationData":[TD([[makeQuery(id+"F0.imprint","IMPRINT",EDGE,{"derivedFrom":sQuery(id+"F0.wireOp",EDGE,"E32.MirrorCS")}),-1.0]])]});
            var Q1;
            Q1=makeQuery(id+"F0.imprint","IMPRINT",FACE,{"disambiguationData":[TD([[makeQuery(id+"F0.imprint","IMPRINT",EDGE,{"derivedFrom":sQuery(id+"F0.wireOp",EDGE,"E35.MirrorCS")}),1.0]])]});
            var Q2;
            {var subQ5=sQuery(id+"F0.wireOp",EDGE,"E18.MirrorCS");Q2=makeQuery(id+"F0.imprint","IMPRINT",FACE,{"disambiguationData":[TD([[makeQuery(id+"F0.imprint","IMPRINT",EDGE,{"derivedFrom":subQ5}),-1.0]])]});}
            var Q3;
            {var subQ5=sQuery(id+"F0.wireOp",EDGE,"E13.MirrorCS");Q3=makeQuery(id+"F0.imprint","IMPRINT",FACE,{"disambiguationData":[TD([[makeQuery(id+"F0.imprint","IMPRINT",EDGE,{"derivedFrom":subQ5}),1.0]])]});}
            var Q4;
            {var subQ0=sQuery(id+"F0.wireOp",EDGE,"E8");Q4=makeQuery(id+"F0.imprint","IMPRINT",FACE,{"disambiguationData":[TD([[makeQuery(id+"F0.imprint","IMPRINT",EDGE,{"derivedFrom":subQ0}),-1.0]])]});}
            var Q5;
            Q5=makeQuery(id+"F0.imprint","IMPRINT",FACE,{"disambiguationData":[TD([[makeQuery(id+"F0.imprint","IMPRINT",EDGE,{"derivedFrom":sQuery(id+"F0.wireOp",EDGE,"E19.MirrorCS")}),1.0]])]});
            var Q6;
            {var subQ0=sQuery(id+"F0.wireOp",EDGE,"E26");Q6=makeQuery(id+"F0.imprint","IMPRINT",FACE,{"disambiguationData":[TD([[makeQuery(id+"F0.imprint","IMPRINT",EDGE,{"derivedFrom":subQ0}),1.0]])]});}
            var Q7;
            {var subQ5=sQuery(id+"F0.wireOp",EDGE,"E30.MirrorCS");Q7=makeQuery(id+"F0.imprint","IMPRINT",FACE,{"disambiguationData":[TD([[makeQuery(id+"F0.imprint","IMPRINT",EDGE,{"derivedFrom":subQ5}),-1.0]])]});}
            var Q8;
            Q8=makeQuery(id+"F0.imprint","IMPRINT",FACE,{"disambiguationData":[TD([[makeQuery(id+"F0.imprint","IMPRINT",EDGE,{"derivedFrom":sQuery(id+"F0.wireOp",EDGE,"E70.MirrorCS")}),-1.0]])]});
            var Q9;
            Q9=makeQuery(id+"F0.imprint","IMPRINT",FACE,{"disambiguationData":[TD([[makeQuery(id+"F0.imprint","IMPRINT",EDGE,{"derivedFrom":sQuery(id+"F0.wireOp",EDGE,"E73.MirrorCS")}),1.0]])]});
            var Q10;
            {var subQ5=sQuery(id+"F0.wireOp",EDGE,"E56.MirrorCS");Q10=makeQuery(id+"F0.imprint","IMPRINT",FACE,{"disambiguationData":[TD([[makeQuery(id+"F0.imprint","IMPRINT",EDGE,{"derivedFrom":subQ5}),-1.0]])]});}
            var Q11;
            {var subQ5=sQuery(id+"F0.wireOp",EDGE,"E51.MirrorCS");Q11=makeQuery(id+"F0.imprint","IMPRINT",FACE,{"disambiguationData":[TD([[makeQuery(id+"F0.imprint","IMPRINT",EDGE,{"derivedFrom":subQ5}),1.0]])]});}
            var Q12;
            {var subQ0=sQuery(id+"F0.wireOp",EDGE,"E46");Q12=makeQuery(id+"F0.imprint","IMPRINT",FACE,{"disambiguationData":[TD([[makeQuery(id+"F0.imprint","IMPRINT",EDGE,{"derivedFrom":subQ0}),-1.0]])]});}
            var Q13;
            Q13=makeQuery(id+"F0.imprint","IMPRINT",FACE,{"disambiguationData":[TD([[makeQuery(id+"F0.imprint","IMPRINT",EDGE,{"derivedFrom":sQuery(id+"F0.wireOp",EDGE,"E57.MirrorCS")}),1.0]])]});
            var Q14;
            {var subQ0=sQuery(id+"F0.wireOp",EDGE,"E64");Q14=makeQuery(id+"F0.imprint","IMPRINT",FACE,{"disambiguationData":[TD([[makeQuery(id+"F0.imprint","IMPRINT",EDGE,{"derivedFrom":subQ0}),1.0]])]});}
            var Q15;
            {var subQ5=sQuery(id+"F0.wireOp",EDGE,"E68.MirrorCS");Q15=makeQuery(id+"F0.imprint","IMPRINT",FACE,{"disambiguationData":[TD([[makeQuery(id+"F0.imprint","IMPRINT",EDGE,{"derivedFrom":subQ5}),-1.0]])]});}
            var Q16;
            {var subQ0=sQuery(id+"F0.wireOp",EDGE,"E170.MirrorCS");Q16=makeQuery(id+"F0.imprint","IMPRINT",FACE,{"disambiguationData":[TD([[makeQuery(id+"F0.imprint","IMPRINT",EDGE,{"derivedFrom":subQ0}),-1.0]])]});}
            var Q17;
            {var subQ2=sQuery(id+"F0.wireOp",EDGE,"E173.MirrorCS");Q17=makeQuery(id+"F0.imprint","IMPRINT",FACE,{"disambiguationData":[TD([[makeQuery(id+"F0.imprint","IMPRINT",EDGE,{"derivedFrom":subQ2}),1.0]])]});}
            var Q18;
            {var subQ0=sQuery(id+"F0.wireOp",EDGE,"E160.MirrorCS");Q18=makeQuery(id+"F0.imprint","IMPRINT",FACE,{"disambiguationData":[TD([[makeQuery(id+"F0.imprint","IMPRINT",EDGE,{"derivedFrom":subQ0}),1.0]])]});}
            var Q19;
            {var subQ0=sQuery(id+"F0.wireOp",EDGE,"E163.MirrorCS");Q19=makeQuery(id+"F0.imprint","IMPRINT",FACE,{"disambiguationData":[TD([[makeQuery(id+"F0.imprint","IMPRINT",EDGE,{"derivedFrom":subQ0}),-1.0]])]});}
            var Q20;
            {var subQ2=sQuery(id+"F0.wireOp",EDGE,"E4");var subQ18=makeQuery(id+"F0.imprint","INTERSECT",VERTEX,{"derivedFrom":[subQ2,sQuery(id+"F0.wireOp",EDGE,"E39")]});Q20=makeQuery(id+"F0.imprint","IMPRINT",FACE,{"disambiguationData":[TD([[makeQuery(id+"F0.imprint","IMPRINT",EDGE,{"disambiguationData":[TD([[subQ18,-1.0]])],"derivedFrom":subQ2}),1.0]])]});}
            var Q21;
            {var subQ2=sQuery(id+"F0.wireOp",EDGE,"E42");var subQ18=makeQuery(id+"F0.imprint","INTERSECT",VERTEX,{"derivedFrom":[subQ2,sQuery(id+"F0.wireOp",EDGE,"E77")]});Q21=makeQuery(id+"F0.imprint","IMPRINT",FACE,{"disambiguationData":[TD([[makeQuery(id+"F0.imprint","IMPRINT",EDGE,{"disambiguationData":[TD([[subQ18,-1.0]])],"derivedFrom":subQ2}),1.0]])]});}
            var Q22;
            {var subQ21=sQuery(id+"F0.wireOp",EDGE,"9dO9B8TU-6T6k-28fZ-blXv-dWgkXBQdFVAd");Q22=makeQuery(id+"F0.imprint","IMPRINT",FACE,{"disambiguationData":[TD([[makeQuery(id+"F0.imprint","IMPRINT",EDGE,{"derivedFrom":subQ21}),-1.0]])]});}
            var Q23;
            Q23=makeQuery(id+"F0.imprint","IMPRINT",FACE,{"disambiguationData":[TD([[makeQuery(id+"F0.imprint","IMPRINT",EDGE,{"derivedFrom":sQuery(id+"F0.wireOp",EDGE,"E94")}),-1.0]])]});
            var Q24;
            {var subQ7=sQuery(id+"F0.wireOp",EDGE,"E148");Q24=makeQuery(id+"F0.imprint","IMPRINT",FACE,{"disambiguationData":[TD([[makeQuery(id+"F0.imprint","IMPRINT",EDGE,{"derivedFrom":subQ7}),-1.0]])]});}
            extrude(context, id + "F1", {"entities" : qUnion([Q0, Q1, Q2, Q3, Q4, Q5, Q6, Q7, Q8, Q9, Q10, Q11, Q12, Q13, Q14, Q15, Q16, Q17, Q18, Q19, Q20, Q21, Q22, Q23, Q24]), "depth" : 5.08 * mm, "offsetDistance" : 25 * mm});
        }
        {
            var Q0;
            {var subQ7=sQuery(id+"F0.wireOp",EDGE,"E201");Q0=makeQuery(id+"F0.imprint","IMPRINT",FACE,{"disambiguationData":[TD([[makeQuery(id+"F0.imprint","IMPRINT",EDGE,{"derivedFrom":subQ7}),-1.0]])]});}
            var Q1;
            {var subQ0=sQuery(id+"F0.wireOp",EDGE,"E223.MirrorCS");Q1=makeQuery(id+"F0.imprint","IMPRINT",FACE,{"disambiguationData":[TD([[makeQuery(id+"F0.imprint","IMPRINT",EDGE,{"derivedFrom":subQ0}),-1.0]])]});}
            var Q2;
            {var subQ0=sQuery(id+"F0.wireOp",EDGE,"E226.MirrorCS");Q2=makeQuery(id+"F0.imprint","IMPRINT",FACE,{"disambiguationData":[TD([[makeQuery(id+"F0.imprint","IMPRINT",EDGE,{"derivedFrom":subQ0}),1.0]])]});}
            var Q3;
            {var subQ0=sQuery(id+"F0.wireOp",EDGE,"E216.MirrorCS");Q3=makeQuery(id+"F0.imprint","IMPRINT",FACE,{"disambiguationData":[TD([[makeQuery(id+"F0.imprint","IMPRINT",EDGE,{"derivedFrom":subQ0}),-1.0]])]});}
            var Q4;
            {var subQ0=sQuery(id+"F0.wireOp",EDGE,"E213.MirrorCS");Q4=makeQuery(id+"F0.imprint","IMPRINT",FACE,{"disambiguationData":[TD([[makeQuery(id+"F0.imprint","IMPRINT",EDGE,{"derivedFrom":subQ0}),1.0]])]});}
            extrude(context, id + "F2", {"entities" : qUnion([Q0, Q1, Q2, Q3, Q4]), "depth" : 5.07 * mm, "offsetDistance" : 25 * mm});
        }
        {
            var Q0;
            Q0=makeQuery(id+"F0.imprint","IMPRINT",FACE,{"disambiguationData":[TD([[makeQuery(id+"F0.imprint","IMPRINT",EDGE,{"derivedFrom":sQuery(id+"F0.wireOp",EDGE,"E260")}),-1.0]])]});
            var Q1;
            {var subQ2=sQuery(id+"F0.wireOp",EDGE,"E320");Q1=makeQuery(id+"F0.imprint","IMPRINT",FACE,{"disambiguationData":[TD([[makeQuery(id+"F0.imprint","IMPRINT",EDGE,{"derivedFrom":subQ2}),-1.0]])]});}
            var Q2;
            {var subQ0=sQuery(id+"F0.wireOp",EDGE,"E336.MirrorCS");var subQ1=sQuery(id+"F0.wireOp",EDGE,"E314");var subQ2=makeQuery(id+"F0.imprint","INTERSECT",VERTEX,{"derivedFrom":[subQ1,subQ0]});Q2=makeQuery(id+"F0.imprint","IMPRINT",FACE,{"disambiguationData":[TD([[makeQuery(id+"F0.imprint","IMPRINT",EDGE,{"disambiguationData":[TD([[subQ2,1.0]])],"derivedFrom":subQ0}),1.0]])]});}
            var Q3;
            {var subQ3=sQuery(id+"F0.wireOp",EDGE,"E341.MirrorCS");var subQ5=sQuery(id+"F0.wireOp",EDGE,"E345.MirrorCS");var subQ6=makeQuery(id+"F0.imprint","INTERSECT",VERTEX,{"derivedFrom":[subQ3,subQ5]});Q3=makeQuery(id+"F0.imprint","IMPRINT",FACE,{"disambiguationData":[TD([[makeQuery(id+"F0.imprint","IMPRINT",EDGE,{"disambiguationData":[TD([[subQ6,-1.0]])],"derivedFrom":subQ3}),-1.0]])]});}
            var Q4;
            {var subQ0=sQuery(id+"F0.wireOp",EDGE,"E348");Q4=makeQuery(id+"F0.imprint","IMPRINT",FACE,{"disambiguationData":[TD([[makeQuery(id+"F0.imprint","IMPRINT",EDGE,{"derivedFrom":subQ0}),-1.0]])]});}
            var Q5;
            {var subQ0=sQuery(id+"F0.wireOp",EDGE,"E351");Q5=makeQuery(id+"F0.imprint","IMPRINT",FACE,{"disambiguationData":[TD([[makeQuery(id+"F0.imprint","IMPRINT",EDGE,{"derivedFrom":subQ0}),-1.0]])]});}
            var Q6;
            {var subQ3=sQuery(id+"F0.wireOp",EDGE,"E330.MirrorCS");var subQ5=sQuery(id+"F0.wireOp",EDGE,"E331.MirrorCS");var subQ7=makeQuery(id+"F0.imprint","INTERSECT",VERTEX,{"derivedFrom":[subQ3,subQ5]});Q6=makeQuery(id+"F0.imprint","IMPRINT",FACE,{"disambiguationData":[TD([[makeQuery(id+"F0.imprint","IMPRINT",EDGE,{"disambiguationData":[TD([[subQ7,-1.0]])],"derivedFrom":subQ3}),-1.0]])]});}
            var Q7;
            {var subQ3=sQuery(id+"F0.wireOp",EDGE,"E322");var subQ5=sQuery(id+"F0.wireOp",EDGE,"E325");var subQ6=makeQuery(id+"F0.imprint","INTERSECT",VERTEX,{"derivedFrom":[subQ3,subQ5]});Q7=makeQuery(id+"F0.imprint","IMPRINT",FACE,{"disambiguationData":[TD([[makeQuery(id+"F0.imprint","IMPRINT",EDGE,{"disambiguationData":[TD([[subQ6,-1.0]])],"derivedFrom":subQ3}),-1.0]])]});}
            var Q8;
            {var subQ4=sQuery(id+"F0.wireOp",EDGE,"E346");Q8=makeQuery(id+"F0.imprint","IMPRINT",FACE,{"disambiguationData":[TD([[makeQuery(id+"F0.imprint","IMPRINT",EDGE,{"derivedFrom":subQ4}),-1.0]])]});}
            var Q9;
            {var subQ8=sQuery(id+"F0.wireOp",EDGE,"E346");Q9=makeQuery(id+"F0.imprint","IMPRINT",FACE,{"disambiguationData":[TD([[makeQuery(id+"F0.imprint","IMPRINT",EDGE,{"derivedFrom":subQ8}),1.0]])]});}
            extrude(context, id + "F3", {"entities" : qUnion([Q0, Q1, Q2, Q3, Q4, Q5, Q6, Q7, Q8, Q9]), "depth" : 5.08 * mm, "offsetDistance" : 25 * mm});
        }
        {
            var Q0;
            {var subQ2=sQuery(id+"F0.wireOp",EDGE,"E368");Q0=makeQuery(id+"F0.imprint","IMPRINT",FACE,{"disambiguationData":[TD([[makeQuery(id+"F0.imprint","IMPRINT",EDGE,{"derivedFrom":subQ2}),-1.0]])]});}
            var Q1;
            {var subQ0=sQuery(id+"F0.wireOp",EDGE,"E396");Q1=makeQuery(id+"F0.imprint","IMPRINT",FACE,{"disambiguationData":[TD([[makeQuery(id+"F0.imprint","IMPRINT",EDGE,{"derivedFrom":subQ0}),-1.0]])]});}
            var Q2;
            {var subQ0=sQuery(id+"F0.wireOp",EDGE,"E384.MirrorCS");var subQ1=sQuery(id+"F0.wireOp",EDGE,"E362");var subQ2=makeQuery(id+"F0.imprint","INTERSECT",VERTEX,{"derivedFrom":[subQ1,subQ0]});Q2=makeQuery(id+"F0.imprint","IMPRINT",FACE,{"disambiguationData":[TD([[makeQuery(id+"F0.imprint","IMPRINT",EDGE,{"disambiguationData":[TD([[subQ2,1.0]])],"derivedFrom":subQ0}),1.0]])]});}
            var Q3;
            {var subQ8=sQuery(id+"F0.wireOp",EDGE,"E394");Q3=makeQuery(id+"F0.imprint","IMPRINT",FACE,{"disambiguationData":[TD([[makeQuery(id+"F0.imprint","IMPRINT",EDGE,{"derivedFrom":subQ8}),1.0]])]});}
            var Q4;
            {var subQ3=sQuery(id+"F0.wireOp",EDGE,"E370");var subQ5=sQuery(id+"F0.wireOp",EDGE,"E373");var subQ6=makeQuery(id+"F0.imprint","INTERSECT",VERTEX,{"derivedFrom":[subQ3,subQ5]});Q4=makeQuery(id+"F0.imprint","IMPRINT",FACE,{"disambiguationData":[TD([[makeQuery(id+"F0.imprint","IMPRINT",EDGE,{"disambiguationData":[TD([[subQ6,-1.0]])],"derivedFrom":subQ3}),-1.0]])]});}
            var Q5;
            {var subQ4=sQuery(id+"F0.wireOp",EDGE,"E394");Q5=makeQuery(id+"F0.imprint","IMPRINT",FACE,{"disambiguationData":[TD([[makeQuery(id+"F0.imprint","IMPRINT",EDGE,{"derivedFrom":subQ4}),-1.0]])]});}
            var Q6;
            {var subQ3=sQuery(id+"F0.wireOp",EDGE,"E378.MirrorCS");var subQ5=sQuery(id+"F0.wireOp",EDGE,"E379.MirrorCS");var subQ7=makeQuery(id+"F0.imprint","INTERSECT",VERTEX,{"derivedFrom":[subQ3,subQ5]});Q6=makeQuery(id+"F0.imprint","IMPRINT",FACE,{"disambiguationData":[TD([[makeQuery(id+"F0.imprint","IMPRINT",EDGE,{"disambiguationData":[TD([[subQ7,-1.0]])],"derivedFrom":subQ3}),-1.0]])]});}
            var Q7;
            {var subQ3=sQuery(id+"F0.wireOp",EDGE,"E389.MirrorCS");var subQ5=sQuery(id+"F0.wireOp",EDGE,"E393.MirrorCS");var subQ6=makeQuery(id+"F0.imprint","INTERSECT",VERTEX,{"derivedFrom":[subQ3,subQ5]});Q7=makeQuery(id+"F0.imprint","IMPRINT",FACE,{"disambiguationData":[TD([[makeQuery(id+"F0.imprint","IMPRINT",EDGE,{"disambiguationData":[TD([[subQ6,-1.0]])],"derivedFrom":subQ3}),-1.0]])]});}
            var Q8;
            {var subQ0=sQuery(id+"F0.wireOp",EDGE,"E399");Q8=makeQuery(id+"F0.imprint","IMPRINT",FACE,{"disambiguationData":[TD([[makeQuery(id+"F0.imprint","IMPRINT",EDGE,{"derivedFrom":subQ0}),-1.0]])]});}
            extrude(context, id + "F4", {"entities" : qUnion([Q0, Q1, Q2, Q3, Q4, Q5, Q6, Q7, Q8]), "depth" : 5.08 * mm, "offsetDistance" : 25 * mm});
        }
    });
